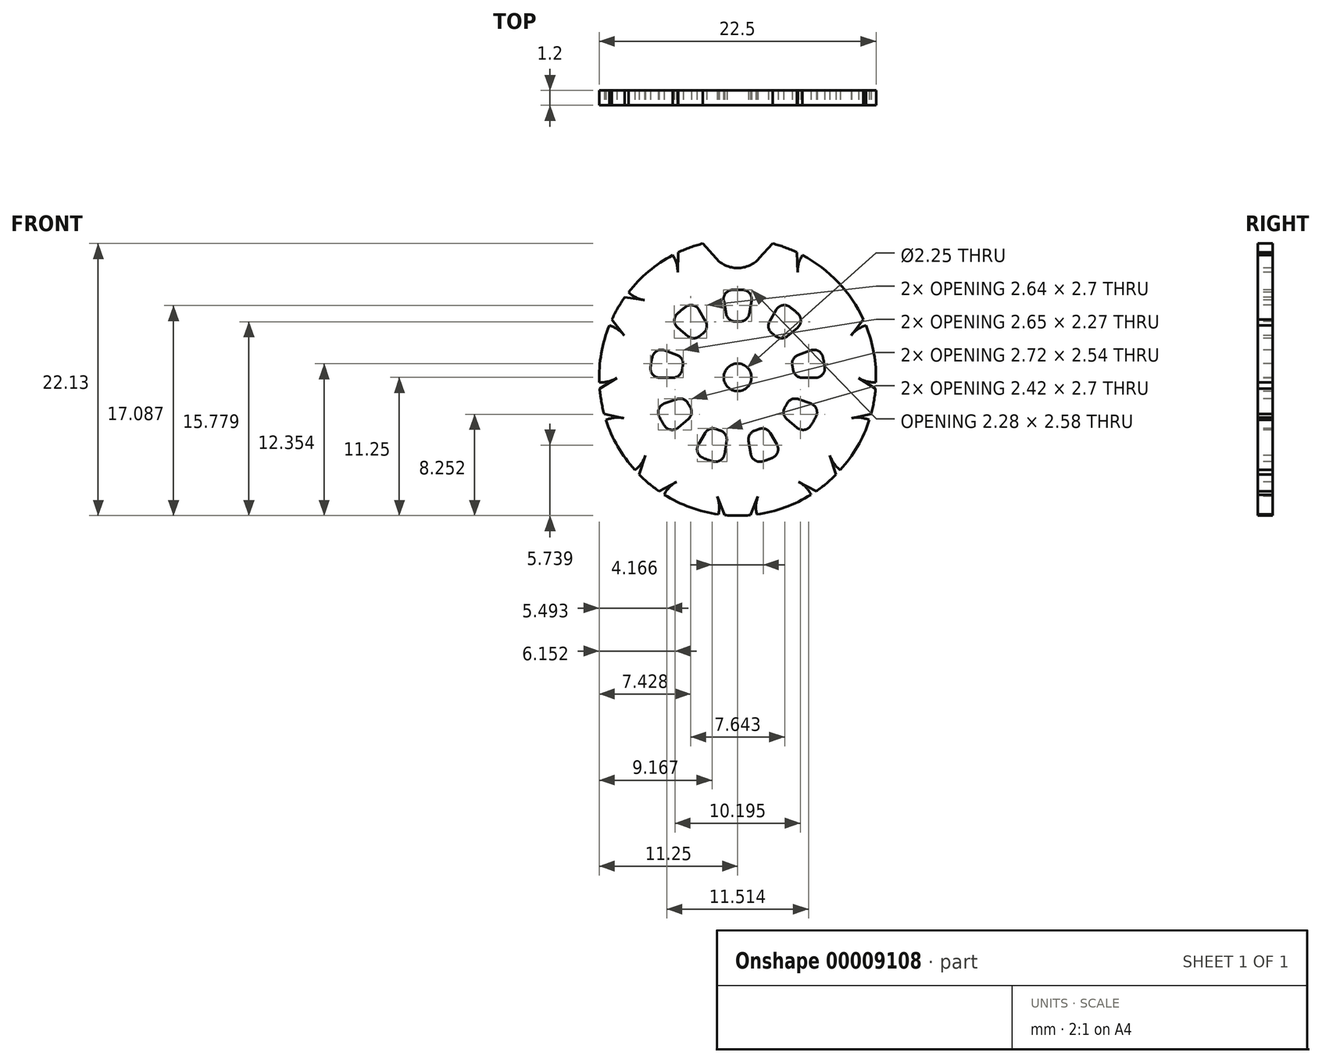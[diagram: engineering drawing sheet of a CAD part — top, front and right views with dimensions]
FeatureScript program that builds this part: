
annotation { "Feature Type Name" : "Feature", "Feature Type Description" : "" }
export const myFeature = defineFeature(function(context is Context, id is Id, definition is map)
    precondition{}
    {
        {
            var Q0;
            Q0=qCreatedBy(makeId("Front.planeOp"),FACE);
            var sketch = newSketch(context, id + "F0", { "sketchPlane" : qUnion([Q0])});
            skCircle(sketch, "E0", {"center": v(0, 0) * mm, "radius": 7.5 * mm});
            skSolve(sketch);
        }
        {
            var Q0;
            Q0 = qSketchRegion(id + "F0", true);
            extrude(context, id + "F1", {"entities" : qUnion([Q0]), "depth" : 0.8 * mm});
        }
        {
            var Q0;
            Q0=makeQuery(id+"F1.opExtrude","CAP_FACE",FACE,{"disambiguationData":[OSD([sQuery(id+"F0.wireOp",EDGE,"E0")])],"isStart":false});
            var sketch = newSketch(context, id + "F2", { "sketchPlane" : qUnion([Q0])});
            skCircle(sketch, "E1", {"center": v(0, 7.5) * mm, "radius": 1.57 * mm});
            skCircle(sketch, "E2", {"center": v(4.82, 5.75) * mm, "radius": 1.57 * mm});
            skLineSegment(sketch, "E3", {"start": v(0, 0) * mm, "end": v(4.82, 5.75) * mm, "construction": true});
            skLineSegment(sketch, "E4", {"start": v(0, 7.5) * mm, "end": v(4.82, 5.75) * mm, "construction": true});
            skLineSegment(sketch, "E5", {"start": v(0, 0) * mm, "end": v(2.41, 6.62) * mm, "construction": true});
            skLineSegment(sketch, "E6", {"start": v(2.23, 7.63) * mm, "end": v(1.17, 6.45) * mm});
            skLineSegment(sketch, "E7.MirrorCS", {"start": v(3.2, 7.28) * mm, "end": v(3.25, 5.7) * mm});
            skLineSegment(sketch, "E8", {"start": v(2.23, 7.63) * mm, "end": v(3.2, 7.28) * mm});
            skCircle(sketch, "E9.1.0", {"center": v(-4.82, 5.75) * mm, "radius": 1.57 * mm});
            skLineSegment(sketch, "E9.1.1", {"start": v(-3.2, 7.28) * mm, "end": v(-3.25, 5.7) * mm});
            skLineSegment(sketch, "E9.1.2", {"start": v(-3.2, 7.28) * mm, "end": v(-2.23, 7.63) * mm});
            skLineSegment(sketch, "E9.1.3", {"start": v(-2.23, 7.63) * mm, "end": v(-1.17, 6.45) * mm});
            skCircle(sketch, "E9.2.0", {"center": v(-7.39, 1.3) * mm, "radius": 1.57 * mm});
            skLineSegment(sketch, "E9.2.1", {"start": v(-7.13, 3.52) * mm, "end": v(-6.15, 2.27) * mm});
            skLineSegment(sketch, "E9.2.2", {"start": v(-7.13, 3.52) * mm, "end": v(-6.61, 4.41) * mm});
            skLineSegment(sketch, "E9.2.3", {"start": v(-6.61, 4.41) * mm, "end": v(-5.04, 4.19) * mm});
            skCircle(sketch, "E9.2.4", {"center": v(-4.82, 5.75) * mm, "radius": 1.57 * mm});
            skCircle(sketch, "E9.3.0", {"center": v(-6.5, -3.75) * mm, "radius": 1.57 * mm});
            skLineSegment(sketch, "E9.3.1", {"start": v(-7.72, -1.88) * mm, "end": v(-6.17, -2.21) * mm});
            skLineSegment(sketch, "E9.3.2", {"start": v(-7.72, -1.88) * mm, "end": v(-7.9, -0.87) * mm});
            skLineSegment(sketch, "E9.3.3", {"start": v(-7.9, -0.87) * mm, "end": v(-6.55, -0.03) * mm});
            skCircle(sketch, "E9.3.4", {"center": v(-7.39, 1.3) * mm, "radius": 1.57 * mm});
            skCircle(sketch, "E9.4.0", {"center": v(-2.57, -7.05) * mm, "radius": 1.57 * mm});
            skLineSegment(sketch, "E9.4.1", {"start": v(-4.7, -6.4) * mm, "end": v(-3.3, -5.66) * mm});
            skLineSegment(sketch, "E9.4.2", {"start": v(-4.7, -6.4) * mm, "end": v(-5.5, -5.74) * mm});
            skLineSegment(sketch, "E9.4.3", {"start": v(-5.5, -5.74) * mm, "end": v(-5, -4.24) * mm});
            skCircle(sketch, "E9.4.4", {"center": v(-6.5, -3.75) * mm, "radius": 1.57 * mm});
            skCircle(sketch, "E9.5.0", {"center": v(2.57, -7.05) * mm, "radius": 1.57 * mm});
            skLineSegment(sketch, "E9.5.1", {"start": v(0.51, -7.93) * mm, "end": v(1.1, -6.46) * mm});
            skLineSegment(sketch, "E9.5.2", {"start": v(0.51, -7.93) * mm, "end": v(-0.51, -7.93) * mm});
            skLineSegment(sketch, "E9.5.3", {"start": v(-0.51, -7.93) * mm, "end": v(-1.1, -6.46) * mm});
            skCircle(sketch, "E9.5.4", {"center": v(-2.57, -7.05) * mm, "radius": 1.57 * mm});
            skCircle(sketch, "E9.6.0", {"center": v(6.5, -3.75) * mm, "radius": 1.57 * mm});
            skLineSegment(sketch, "E9.6.1", {"start": v(5.5, -5.74) * mm, "end": v(5, -4.24) * mm});
            skLineSegment(sketch, "E9.6.2", {"start": v(5.5, -5.74) * mm, "end": v(4.7, -6.4) * mm});
            skLineSegment(sketch, "E9.6.3", {"start": v(4.7, -6.4) * mm, "end": v(3.3, -5.66) * mm});
            skCircle(sketch, "E9.6.4", {"center": v(2.57, -7.05) * mm, "radius": 1.57 * mm});
            skCircle(sketch, "E9.7.0", {"center": v(7.39, 1.3) * mm, "radius": 1.57 * mm});
            skLineSegment(sketch, "E9.7.1", {"start": v(7.9, -0.87) * mm, "end": v(6.55, -0.03) * mm});
            skLineSegment(sketch, "E9.7.2", {"start": v(7.9, -0.87) * mm, "end": v(7.72, -1.88) * mm});
            skLineSegment(sketch, "E9.7.3", {"start": v(7.72, -1.88) * mm, "end": v(6.17, -2.21) * mm});
            skCircle(sketch, "E9.7.4", {"center": v(6.5, -3.75) * mm, "radius": 1.57 * mm});
            skLineSegment(sketch, "E9.8.1", {"start": v(6.61, 4.41) * mm, "end": v(5.04, 4.19) * mm});
            skLineSegment(sketch, "E9.8.2", {"start": v(6.61, 4.41) * mm, "end": v(7.13, 3.52) * mm});
            skLineSegment(sketch, "E9.8.3", {"start": v(7.13, 3.52) * mm, "end": v(6.15, 2.27) * mm});
            skCircle(sketch, "E9.8.4", {"center": v(7.39, 1.3) * mm, "radius": 1.57 * mm});
            skPoint(sketch, "E9.center", {"position": v(0, 0) * mm});
            skSolve(sketch);
        }
        {
            var Q0;
            {var subQ1=sQuery(id+"F2.wireOp",EDGE,"E1");var subQ5=makeQuery(id+"F2.imprint","INTERSECT",VERTEX,{"derivedFrom":[sQuery(id+"F2.wireOp",EDGE,"E9.1.3"),subQ1]});Q0=makeQuery(id+"F2.imprint","IMPRINT",FACE,{"disambiguationData":[TD([[makeQuery(id+"F2.imprint","IMPRINT",EDGE,{"disambiguationData":[TD([[subQ5,1.0]])],"derivedFrom":subQ1}),1.0]])]});}
            var Q1;
            {var subQ1=sQuery(id+"F2.wireOp",EDGE,"E1");var subQ3=sQuery(id+"F2.wireOp",EDGE,"E6");var subQ5=makeQuery(id+"F2.imprint","INTERSECT",VERTEX,{"derivedFrom":[subQ3,subQ1]});Q1=makeQuery(id+"F2.imprint","IMPRINT",FACE,{"disambiguationData":[TD([[makeQuery(id+"F2.imprint","IMPRINT",EDGE,{"disambiguationData":[TD([[subQ5,1.0]])],"derivedFrom":subQ3}),-1.0]])]});}
            var Q2;
            {var subQ1=sQuery(id+"F2.wireOp",EDGE,"E2");var subQ3=sQuery(id+"F2.wireOp",EDGE,"E7.MirrorCS");var subQ5=makeQuery(id+"F2.imprint","INTERSECT",VERTEX,{"derivedFrom":[subQ3,subQ1]});Q2=makeQuery(id+"F2.imprint","IMPRINT",FACE,{"disambiguationData":[TD([[makeQuery(id+"F2.imprint","IMPRINT",EDGE,{"disambiguationData":[TD([[subQ5,1.0]])],"derivedFrom":subQ3}),1.0]])]});}
            var Q3;
            {var subQ1=sQuery(id+"F2.wireOp",EDGE,"E2");var subQ5=makeQuery(id+"F2.imprint","INTERSECT",VERTEX,{"derivedFrom":[sQuery(id+"F2.wireOp",EDGE,"E7.MirrorCS"),subQ1]});Q3=makeQuery(id+"F2.imprint","IMPRINT",FACE,{"disambiguationData":[TD([[makeQuery(id+"F2.imprint","IMPRINT",EDGE,{"disambiguationData":[TD([[subQ5,1.0]])],"derivedFrom":subQ1}),1.0]])]});}
            var Q4;
            {var subQ1=sQuery(id+"F2.wireOp",EDGE,"E9.8.1");var subQ3=sQuery(id+"F2.wireOp",EDGE,"E2");var subQ5=makeQuery(id+"F2.imprint","INTERSECT",VERTEX,{"derivedFrom":[subQ3,subQ1]});Q4=makeQuery(id+"F2.imprint","IMPRINT",FACE,{"disambiguationData":[TD([[makeQuery(id+"F2.imprint","IMPRINT",EDGE,{"disambiguationData":[TD([[subQ5,-1.0]])],"derivedFrom":subQ3}),-1.0]])]});}
            var Q5;
            {var subQ1=sQuery(id+"F2.wireOp",EDGE,"E9.8.4");var subQ3=sQuery(id+"F2.wireOp",EDGE,"E9.8.3");var subQ5=makeQuery(id+"F2.imprint","INTERSECT",VERTEX,{"derivedFrom":[subQ3,subQ1]});Q5=makeQuery(id+"F2.imprint","IMPRINT",FACE,{"disambiguationData":[TD([[makeQuery(id+"F2.imprint","IMPRINT",EDGE,{"disambiguationData":[TD([[subQ5,1.0]])],"derivedFrom":subQ3}),1.0]])]});}
            var Q6;
            {var subQ1=sQuery(id+"F2.wireOp",EDGE,"E9.8.4");var subQ5=makeQuery(id+"F2.imprint","INTERSECT",VERTEX,{"derivedFrom":[sQuery(id+"F2.wireOp",EDGE,"E9.8.3"),subQ1]});Q6=makeQuery(id+"F2.imprint","IMPRINT",FACE,{"disambiguationData":[TD([[makeQuery(id+"F2.imprint","IMPRINT",EDGE,{"disambiguationData":[TD([[subQ5,1.0]])],"derivedFrom":subQ1}),1.0]])]});}
            var Q7;
            {var subQ1=sQuery(id+"F2.wireOp",EDGE,"E9.8.4");var subQ3=sQuery(id+"F2.wireOp",EDGE,"E9.7.1");var subQ5=makeQuery(id+"F2.imprint","INTERSECT",VERTEX,{"derivedFrom":[subQ3,subQ1]});Q7=makeQuery(id+"F2.imprint","IMPRINT",FACE,{"disambiguationData":[TD([[makeQuery(id+"F2.imprint","IMPRINT",EDGE,{"disambiguationData":[TD([[subQ5,1.0]])],"derivedFrom":subQ3}),-1.0]])]});}
            var Q8;
            {var subQ1=sQuery(id+"F2.wireOp",EDGE,"E9.7.4");var subQ3=sQuery(id+"F2.wireOp",EDGE,"E9.7.3");var subQ5=makeQuery(id+"F2.imprint","INTERSECT",VERTEX,{"derivedFrom":[subQ3,subQ1]});Q8=makeQuery(id+"F2.imprint","IMPRINT",FACE,{"disambiguationData":[TD([[makeQuery(id+"F2.imprint","IMPRINT",EDGE,{"disambiguationData":[TD([[subQ5,1.0]])],"derivedFrom":subQ3}),1.0]])]});}
            var Q9;
            {var subQ1=sQuery(id+"F2.wireOp",EDGE,"E9.7.4");var subQ5=makeQuery(id+"F2.imprint","INTERSECT",VERTEX,{"derivedFrom":[sQuery(id+"F2.wireOp",EDGE,"E9.7.3"),subQ1]});Q9=makeQuery(id+"F2.imprint","IMPRINT",FACE,{"disambiguationData":[TD([[makeQuery(id+"F2.imprint","IMPRINT",EDGE,{"disambiguationData":[TD([[subQ5,1.0]])],"derivedFrom":subQ1}),1.0]])]});}
            var Q10;
            {var subQ1=sQuery(id+"F2.wireOp",EDGE,"E9.7.4");var subQ3=sQuery(id+"F2.wireOp",EDGE,"E9.6.1");var subQ5=makeQuery(id+"F2.imprint","INTERSECT",VERTEX,{"derivedFrom":[subQ3,subQ1]});Q10=makeQuery(id+"F2.imprint","IMPRINT",FACE,{"disambiguationData":[TD([[makeQuery(id+"F2.imprint","IMPRINT",EDGE,{"disambiguationData":[TD([[subQ5,1.0]])],"derivedFrom":subQ3}),-1.0]])]});}
            var Q11;
            {var subQ1=sQuery(id+"F2.wireOp",EDGE,"E9.6.4");var subQ3=sQuery(id+"F2.wireOp",EDGE,"E9.6.3");var subQ5=makeQuery(id+"F2.imprint","INTERSECT",VERTEX,{"derivedFrom":[subQ3,subQ1]});Q11=makeQuery(id+"F2.imprint","IMPRINT",FACE,{"disambiguationData":[TD([[makeQuery(id+"F2.imprint","IMPRINT",EDGE,{"disambiguationData":[TD([[subQ5,1.0]])],"derivedFrom":subQ3}),1.0]])]});}
            var Q12;
            {var subQ1=sQuery(id+"F2.wireOp",EDGE,"E9.6.4");var subQ5=makeQuery(id+"F2.imprint","INTERSECT",VERTEX,{"derivedFrom":[sQuery(id+"F2.wireOp",EDGE,"E9.6.3"),subQ1]});Q12=makeQuery(id+"F2.imprint","IMPRINT",FACE,{"disambiguationData":[TD([[makeQuery(id+"F2.imprint","IMPRINT",EDGE,{"disambiguationData":[TD([[subQ5,1.0]])],"derivedFrom":subQ1}),1.0]])]});}
            var Q13;
            {var subQ1=sQuery(id+"F2.wireOp",EDGE,"E9.6.4");var subQ3=sQuery(id+"F2.wireOp",EDGE,"E9.5.1");var subQ5=makeQuery(id+"F2.imprint","INTERSECT",VERTEX,{"derivedFrom":[subQ3,subQ1]});Q13=makeQuery(id+"F2.imprint","IMPRINT",FACE,{"disambiguationData":[TD([[makeQuery(id+"F2.imprint","IMPRINT",EDGE,{"disambiguationData":[TD([[subQ5,1.0]])],"derivedFrom":subQ3}),-1.0]])]});}
            var Q14;
            {var subQ1=sQuery(id+"F2.wireOp",EDGE,"E9.5.4");var subQ3=sQuery(id+"F2.wireOp",EDGE,"E9.5.3");var subQ5=makeQuery(id+"F2.imprint","INTERSECT",VERTEX,{"derivedFrom":[subQ3,subQ1]});Q14=makeQuery(id+"F2.imprint","IMPRINT",FACE,{"disambiguationData":[TD([[makeQuery(id+"F2.imprint","IMPRINT",EDGE,{"disambiguationData":[TD([[subQ5,1.0]])],"derivedFrom":subQ3}),1.0]])]});}
            var Q15;
            {var subQ1=sQuery(id+"F2.wireOp",EDGE,"E9.5.4");var subQ5=makeQuery(id+"F2.imprint","INTERSECT",VERTEX,{"derivedFrom":[sQuery(id+"F2.wireOp",EDGE,"E9.5.3"),subQ1]});Q15=makeQuery(id+"F2.imprint","IMPRINT",FACE,{"disambiguationData":[TD([[makeQuery(id+"F2.imprint","IMPRINT",EDGE,{"disambiguationData":[TD([[subQ5,1.0]])],"derivedFrom":subQ1}),1.0]])]});}
            var Q16;
            {var subQ1=sQuery(id+"F2.wireOp",EDGE,"E9.5.4");var subQ3=sQuery(id+"F2.wireOp",EDGE,"E9.4.1");var subQ5=makeQuery(id+"F2.imprint","INTERSECT",VERTEX,{"derivedFrom":[subQ3,subQ1]});Q16=makeQuery(id+"F2.imprint","IMPRINT",FACE,{"disambiguationData":[TD([[makeQuery(id+"F2.imprint","IMPRINT",EDGE,{"disambiguationData":[TD([[subQ5,1.0]])],"derivedFrom":subQ3}),-1.0]])]});}
            var Q17;
            {var subQ1=sQuery(id+"F2.wireOp",EDGE,"E9.4.4");var subQ3=sQuery(id+"F2.wireOp",EDGE,"E9.4.3");var subQ5=makeQuery(id+"F2.imprint","INTERSECT",VERTEX,{"derivedFrom":[subQ3,subQ1]});Q17=makeQuery(id+"F2.imprint","IMPRINT",FACE,{"disambiguationData":[TD([[makeQuery(id+"F2.imprint","IMPRINT",EDGE,{"disambiguationData":[TD([[subQ5,1.0]])],"derivedFrom":subQ3}),1.0]])]});}
            var Q18;
            {var subQ1=sQuery(id+"F2.wireOp",EDGE,"E9.4.4");var subQ5=makeQuery(id+"F2.imprint","INTERSECT",VERTEX,{"derivedFrom":[sQuery(id+"F2.wireOp",EDGE,"E9.4.3"),subQ1]});Q18=makeQuery(id+"F2.imprint","IMPRINT",FACE,{"disambiguationData":[TD([[makeQuery(id+"F2.imprint","IMPRINT",EDGE,{"disambiguationData":[TD([[subQ5,1.0]])],"derivedFrom":subQ1}),1.0]])]});}
            var Q19;
            {var subQ1=sQuery(id+"F2.wireOp",EDGE,"E9.4.4");var subQ3=sQuery(id+"F2.wireOp",EDGE,"E9.3.1");var subQ5=makeQuery(id+"F2.imprint","INTERSECT",VERTEX,{"derivedFrom":[subQ3,subQ1]});Q19=makeQuery(id+"F2.imprint","IMPRINT",FACE,{"disambiguationData":[TD([[makeQuery(id+"F2.imprint","IMPRINT",EDGE,{"disambiguationData":[TD([[subQ5,1.0]])],"derivedFrom":subQ3}),-1.0]])]});}
            var Q20;
            {var subQ1=sQuery(id+"F2.wireOp",EDGE,"E9.3.4");var subQ3=sQuery(id+"F2.wireOp",EDGE,"E9.3.3");var subQ5=makeQuery(id+"F2.imprint","INTERSECT",VERTEX,{"derivedFrom":[subQ3,subQ1]});Q20=makeQuery(id+"F2.imprint","IMPRINT",FACE,{"disambiguationData":[TD([[makeQuery(id+"F2.imprint","IMPRINT",EDGE,{"disambiguationData":[TD([[subQ5,1.0]])],"derivedFrom":subQ3}),1.0]])]});}
            var Q21;
            {var subQ1=sQuery(id+"F2.wireOp",EDGE,"E9.3.4");var subQ5=makeQuery(id+"F2.imprint","INTERSECT",VERTEX,{"derivedFrom":[sQuery(id+"F2.wireOp",EDGE,"E9.3.3"),subQ1]});Q21=makeQuery(id+"F2.imprint","IMPRINT",FACE,{"disambiguationData":[TD([[makeQuery(id+"F2.imprint","IMPRINT",EDGE,{"disambiguationData":[TD([[subQ5,1.0]])],"derivedFrom":subQ1}),1.0]])]});}
            var Q22;
            {var subQ1=sQuery(id+"F2.wireOp",EDGE,"E9.3.4");var subQ3=sQuery(id+"F2.wireOp",EDGE,"E9.2.1");var subQ5=makeQuery(id+"F2.imprint","INTERSECT",VERTEX,{"derivedFrom":[subQ3,subQ1]});Q22=makeQuery(id+"F2.imprint","IMPRINT",FACE,{"disambiguationData":[TD([[makeQuery(id+"F2.imprint","IMPRINT",EDGE,{"disambiguationData":[TD([[subQ5,1.0]])],"derivedFrom":subQ3}),-1.0]])]});}
            var Q23;
            {var subQ1=sQuery(id+"F2.wireOp",EDGE,"E9.2.4");var subQ3=sQuery(id+"F2.wireOp",EDGE,"E9.2.3");var subQ5=makeQuery(id+"F2.imprint","INTERSECT",VERTEX,{"derivedFrom":[subQ3,subQ1]});Q23=makeQuery(id+"F2.imprint","IMPRINT",FACE,{"disambiguationData":[TD([[makeQuery(id+"F2.imprint","IMPRINT",EDGE,{"disambiguationData":[TD([[subQ5,1.0]])],"derivedFrom":subQ3}),1.0]])]});}
            var Q24;
            {var subQ1=sQuery(id+"F2.wireOp",EDGE,"E9.2.4");var subQ5=makeQuery(id+"F2.imprint","INTERSECT",VERTEX,{"derivedFrom":[sQuery(id+"F2.wireOp",EDGE,"E9.2.3"),subQ1]});Q24=makeQuery(id+"F2.imprint","IMPRINT",FACE,{"disambiguationData":[TD([[makeQuery(id+"F2.imprint","IMPRINT",EDGE,{"disambiguationData":[TD([[subQ5,1.0]])],"derivedFrom":subQ1}),1.0]])]});}
            var Q25;
            {var subQ1=sQuery(id+"F2.wireOp",EDGE,"E9.2.4");var subQ3=sQuery(id+"F2.wireOp",EDGE,"E9.1.1");var subQ5=makeQuery(id+"F2.imprint","INTERSECT",VERTEX,{"derivedFrom":[subQ3,subQ1]});Q25=makeQuery(id+"F2.imprint","IMPRINT",FACE,{"disambiguationData":[TD([[makeQuery(id+"F2.imprint","IMPRINT",EDGE,{"disambiguationData":[TD([[subQ5,1.0]])],"derivedFrom":subQ3}),-1.0]])]});}
            var Q26;
            {var subQ1=sQuery(id+"F2.wireOp",EDGE,"E1");var subQ3=sQuery(id+"F2.wireOp",EDGE,"E9.1.3");var subQ5=makeQuery(id+"F2.imprint","INTERSECT",VERTEX,{"derivedFrom":[subQ3,subQ1]});Q26=makeQuery(id+"F2.imprint","IMPRINT",FACE,{"disambiguationData":[TD([[makeQuery(id+"F2.imprint","IMPRINT",EDGE,{"disambiguationData":[TD([[subQ5,1.0]])],"derivedFrom":subQ3}),1.0]])]});}
            extrude(context, id + "F3", {"entities" : qUnion([Q0, Q1, Q2, Q3, Q4, Q5, Q6, Q7, Q8, Q9, Q10, Q11, Q12, Q13, Q14, Q15, Q16, Q17, Q18, Q19, Q20, Q21, Q22, Q23, Q24, Q25, Q26]), "operationType" : NewBodyOperationType.REMOVE, "endBound" : BoundingType.THROUGH_ALL, "oppositeDirection" : true, "depth" : 25 * mm});
        }
        {
            var Q0;
            Q0=makeQuery(id+"F1.opExtrude","CAP_FACE",FACE,{"disambiguationData":[OSD([sQuery(id+"F0.wireOp",EDGE,"E0")])],"isStart":false});
            var sketch = newSketch(context, id + "F4", { "sketchPlane" : qUnion([Q0])});
            skLineSegment(sketch, "E10.0.0", {"start": v(6.17, -2.21) * mm, "end": v(7.23, -1.99) * mm});
            skArc(sketch, "E10.0.1", {"start": v(7.23, -1.99) * mm, "mid": v(7.39, -1.3) * mm, "end": v(7.48, -0.6) * mm});
            skLineSegment(sketch, "E10.0.2", {"start": v(7.48, -0.6) * mm, "end": v(6.55, -0.03) * mm});
            skArc(sketch, "E10.0.3", {"start": v(6.55, -0.03) * mm, "mid": v(5.84, 1.03) * mm, "end": v(6.15, 2.27) * mm});
            skLineSegment(sketch, "E10.0.4", {"start": v(6.15, 2.27) * mm, "end": v(6.82, 3.13) * mm});
            skArc(sketch, "E10.0.5", {"start": v(6.82, 3.13) * mm, "mid": v(6.5, 3.75) * mm, "end": v(6.12, 4.34) * mm});
            skLineSegment(sketch, "E10.0.6", {"start": v(6.12, 4.34) * mm, "end": v(5.04, 4.19) * mm});
            skArc(sketch, "E10.0.7", {"start": v(5.04, 4.19) * mm, "mid": v(3.8, 4.54) * mm, "end": v(3.25, 5.7) * mm});
            skLineSegment(sketch, "E10.0.8", {"start": v(3.25, 5.7) * mm, "end": v(3.21, 6.78) * mm});
            skArc(sketch, "E10.0.9", {"start": v(3.21, 6.78) * mm, "mid": v(2.57, 7.05) * mm, "end": v(1.9, 7.26) * mm});
            skLineSegment(sketch, "E10.0.10", {"start": v(1.9, 7.26) * mm, "end": v(1.17, 6.45) * mm});
            skArc(sketch, "E10.0.11", {"start": v(1.17, 6.45) * mm, "mid": v(0, 5.93) * mm, "end": v(-1.17, 6.45) * mm});
            skLineSegment(sketch, "E10.0.12", {"start": v(-1.17, 6.45) * mm, "end": v(-1.9, 7.26) * mm});
            skArc(sketch, "E10.0.13", {"start": v(-1.9, 7.26) * mm, "mid": v(-2.57, 7.05) * mm, "end": v(-3.21, 6.78) * mm});
            skLineSegment(sketch, "E10.0.14", {"start": v(-3.21, 6.78) * mm, "end": v(-3.25, 5.7) * mm});
            skArc(sketch, "E10.0.15", {"start": v(-3.25, 5.7) * mm, "mid": v(-3.8, 4.54) * mm, "end": v(-5.04, 4.19) * mm});
            skLineSegment(sketch, "E10.0.16", {"start": v(-5.04, 4.19) * mm, "end": v(-6.12, 4.34) * mm});
            skArc(sketch, "E10.0.17", {"start": v(-6.12, 4.34) * mm, "mid": v(-6.5, 3.75) * mm, "end": v(-6.82, 3.13) * mm});
            skLineSegment(sketch, "E10.0.18", {"start": v(-6.82, 3.13) * mm, "end": v(-6.15, 2.27) * mm});
            skArc(sketch, "E10.0.19", {"start": v(-6.15, 2.27) * mm, "mid": v(-5.84, 1.03) * mm, "end": v(-6.55, -0.03) * mm});
            skLineSegment(sketch, "E10.0.20", {"start": v(-6.55, -0.03) * mm, "end": v(-7.48, -0.6) * mm});
            skArc(sketch, "E10.0.21", {"start": v(-7.48, -0.6) * mm, "mid": v(-7.39, -1.3) * mm, "end": v(-7.23, -1.99) * mm});
            skLineSegment(sketch, "E10.0.22", {"start": v(-7.23, -1.99) * mm, "end": v(-6.17, -2.21) * mm});
            skArc(sketch, "E10.0.23", {"start": v(-6.17, -2.21) * mm, "mid": v(-5.13, -2.96) * mm, "end": v(-5, -4.24) * mm});
            skLineSegment(sketch, "E10.0.24", {"start": v(-5, -4.24) * mm, "end": v(-5.34, -5.27) * mm});
            skArc(sketch, "E10.0.25", {"start": v(-5.34, -5.27) * mm, "mid": v(-4.82, -5.75) * mm, "end": v(-4.26, -6.17) * mm});
            skLineSegment(sketch, "E10.0.26", {"start": v(-4.26, -6.17) * mm, "end": v(-3.3, -5.66) * mm});
            skArc(sketch, "E10.0.27", {"start": v(-3.3, -5.66) * mm, "mid": v(-2.03, -5.57) * mm, "end": v(-1.1, -6.46) * mm});
            skLineSegment(sketch, "E10.0.28", {"start": v(-1.1, -6.46) * mm, "end": v(-0.7, -7.47) * mm});
            skArc(sketch, "E10.0.29", {"start": v(-0.7, -7.47) * mm, "mid": v(0, -7.5) * mm, "end": v(0.7, -7.47) * mm});
            skLineSegment(sketch, "E10.0.30", {"start": v(0.7, -7.47) * mm, "end": v(1.1, -6.46) * mm});
            skArc(sketch, "E10.0.31", {"start": v(1.1, -6.46) * mm, "mid": v(2.03, -5.57) * mm, "end": v(3.3, -5.66) * mm});
            skLineSegment(sketch, "E10.0.32", {"start": v(3.3, -5.66) * mm, "end": v(4.26, -6.17) * mm});
            skArc(sketch, "E10.0.33", {"start": v(4.26, -6.17) * mm, "mid": v(4.82, -5.75) * mm, "end": v(5.34, -5.27) * mm});
            skLineSegment(sketch, "E10.0.34", {"start": v(5.34, -5.27) * mm, "end": v(5, -4.24) * mm});
            skArc(sketch, "E10.0.35", {"start": v(5, -4.24) * mm, "mid": v(5.13, -2.96) * mm, "end": v(6.17, -2.21) * mm});
            skLineSegment(sketch, "E11", {"start": v(-1.17, 6.45) * mm, "end": v(0, 0) * mm});
            skLineSegment(sketch, "E12", {"start": v(1.17, 6.45) * mm, "end": v(0, 0) * mm});
            skCircle(sketch, "E13", {"center": v(0, 0) * mm, "radius": 3.03 * mm});
            skCircle(sketch, "E14", {"center": v(0, 0) * mm, "radius": 4.75 * mm});
            skSolve(sketch);
        }
        {
            var Q0;
            {var subQ0=sQuery(id+"F4.wireOp",EDGE,"E14");var subQ3=sQuery(id+"F4.wireOp",EDGE,"E11");var subQ4=makeQuery(id+"F4.imprint","INTERSECT",VERTEX,{"derivedFrom":[subQ3,subQ0]});Q0=makeQuery(id+"F4.imprint","IMPRINT",FACE,{"disambiguationData":[TD([[makeQuery(id+"F4.imprint","IMPRINT",EDGE,{"disambiguationData":[TD([[subQ4,-1.0]])],"derivedFrom":subQ3}),1.0]])]});}
            var Q1;
            Q1=makeQuery(id+"F1.opExtrude","CAP_FACE",FACE,{"disambiguationData":[OSD([sQuery(id+"F0.wireOp",EDGE,"E0")])],"isStart":true});
            extrude(context, id + "F5", {"entities" : qUnion([Q0]), "endBound" : BoundingType.UP_TO_SURFACE, "oppositeDirection" : true, "endBoundEntityFace" : qUnion([Q1]), "depth" : 25 * mm});
        }
        {
            var Q0;
            Q0=makeQuery(id+"F5.opExtrude","SWEPT_EDGE",EDGE,{"disambiguationData":[OSD([sQuery(id+"F4.wireOp",EDGE,"E11"),sQuery(id+"F4.wireOp",EDGE,"E14")])]});
            var Q1;
            Q1=makeQuery(id+"F5.opExtrude","SWEPT_EDGE",EDGE,{"disambiguationData":[OSD([sQuery(id+"F4.wireOp",EDGE,"E11"),sQuery(id+"F4.wireOp",EDGE,"E13")])]});
            var Q2;
            Q2=makeQuery(id+"F5.opExtrude","SWEPT_EDGE",EDGE,{"disambiguationData":[OSD([sQuery(id+"F4.wireOp",EDGE,"E12"),sQuery(id+"F4.wireOp",EDGE,"E13")])]});
            var Q3;
            Q3=makeQuery(id+"F5.opExtrude","SWEPT_EDGE",EDGE,{"disambiguationData":[OSD([sQuery(id+"F4.wireOp",EDGE,"E12"),sQuery(id+"F4.wireOp",EDGE,"E14")])]});
            fillet(context, id + "F6", {"entities" : qUnion([Q0, Q1, Q2, Q3]), "radius" : 0.5 * mm, "allowEdgeOverflow" : false});
        }
        {
            var Q0;
            Q0=makeQuery(id+"F5.opExtrude","SWEPT_BODY",BODY,{"disambiguationData":[OSD([sQuery(id+"F4.wireOp",EDGE,"E11"),sQuery(id+"F4.wireOp",EDGE,"E12"),sQuery(id+"F4.wireOp",EDGE,"E13"),sQuery(id+"F4.wireOp",EDGE,"E14")])]});
            var Q1;
            Q1=makeQuery(id+"F5.opExtrude","CAP_EDGE",EDGE,{"disambiguationData":[OSD([sQuery(id+"F4.wireOp",EDGE,"E13")])],"isStart":true});
            circularPattern(context, id + "F7", {"operationType" : NewBodyOperationType.REMOVE, "entities" : qUnion([Q0]), "axis" : qUnion([Q1]), "angle" : 40 * degree, "instanceCount" : 9});
        }
        {
            var Q0;
            Q0=makeQuery(id+"F1.opExtrude","CAP_FACE",FACE,{"disambiguationData":[OSD([sQuery(id+"F0.wireOp",EDGE,"E0")])],"isStart":false});
            var sketch = newSketch(context, id + "F8", { "sketchPlane" : qUnion([Q0])});
            skCircle(sketch, "E15", {"center": v(0, 0) * mm, "radius": 0.75 * mm});
            skSolve(sketch);
        }
        {
            var Q0;
            Q0=makeQuery(id+"F8.imprint","IMPRINT",FACE,{"disambiguationData":[TD([[makeQuery(id+"F8.imprint","IMPRINT",EDGE,{"derivedFrom":sQuery(id+"F8.wireOp",EDGE,"E15")}),1.0]])]});
            extrude(context, id + "F9", {"entities" : qUnion([Q0]), "operationType" : NewBodyOperationType.REMOVE, "endBound" : BoundingType.THROUGH_ALL, "oppositeDirection" : true, "depth" : 25 * mm});
        }
        {
            var Q0;
            Q0=makeQuery(id+"F1.opExtrude","SWEPT_BODY",BODY,{"disambiguationData":[OSD([sQuery(id+"F0.wireOp",EDGE,"E0")])]});
            var Q1;
            Q1=sQuery(id+"F8.wireOp",VERTEX,"E15.center");
            transform(context, id + "F10", {"entities" : qUnion([Q0]), "transformType" : TransformType.SCALE_UNIFORMLY, "scale" : 1.5, "makeCopy" : false, "scalePoint" : qUnion([Q1])});
        }
        {
            var Q0;
            Q0=makeQuery(id+"F1.opExtrude","SWEPT_BODY",BODY,{"disambiguationData":[OSD([sQuery(id+"F0.wireOp",EDGE,"E0")])]});
            transform(context, id + "F11", {"entities" : qUnion([Q0]), "transformType" : TransformType.TRANSLATION_3D, "dx" : 25 * mm, "dy" : 0 * mm, "dz" : 0 * mm, "makeCopy" : true});
        }
        {
            var Q0;
            Q0=makeQuery(id+"F11.opPattern","COPY",BODY,{"derivedFrom":makeQuery(id+"F1.opExtrude","SWEPT_BODY",BODY,{"disambiguationData":[OSD([sQuery(id+"F0.wireOp",EDGE,"E0")])]}),"instanceName":"1"});
            var Q1;
            Q1=makeQuery(id+"F11.opPattern","COPY",VERTEX,{"derivedFrom":makeQuery(id+"F3.boolean.opBoolean","COPY",VERTEX,{"derivedFrom":makeQuery(id+"F3.opExtrude","CAP_VERTEX",VERTEX,{"disambiguationData":[OSD([sQuery(id+"F0.wireOp",EDGE,"E0"),sQuery(id+"F2.wireOp",EDGE,"E9.7.1")])],"isStart":true})}),"instanceName":"1"});
            transform(context, id + "F12", {"entities" : qUnion([Q0]), "transformType" : TransformType.SCALE_UNIFORMLY, "scale" : 0.67, "makeCopy" : false, "scalePoint" : qUnion([Q1])});
        }
        {
            var Q0;
            Q0=makeQuery(id+"F11.opPattern","COPY",BODY,{"derivedFrom":makeQuery(id+"F1.opExtrude","SWEPT_BODY",BODY,{"disambiguationData":[OSD([sQuery(id+"F0.wireOp",EDGE,"E0")])]}),"instanceName":"1"});
            deleteBodies(context, id + "F13", {"entities" : qUnion([Q0])});
        }
    });
